# Revit family: Filter für Warmwasser 0554
name_source: partatom
category: Rohrzubehör
units: mm (PartAtom-declared; Revit-internal decimal feet)

## family parameters
Arbeitsebenenbasiert = Nein
Beim Laden mit Abzugskörper schneiden = Nein
Bemaßung runder Anschluss = Durchmesser verwenden
Gemeinsam genutzt = Nein
Immer vertikal = Ja
OmniClass-Nummer = 23.65.55.14
OmniClass-Titel = Valves for Liquid Services
Teiletyp = Unterbricht

## types (1)
- Filter für Warmwasser 0554
    Ausführung = Der HERZ-Wasserfilter wird in Hauseingangsanlagen für Trinkwasser eingesetzt, um das Trinkwasser vor Verunreinigungen zu schützen.
    D01 = 25.5 mm
    D02 = 22.75 mm  [stored 0.0746391 ft]
    Filter = Edelstahl, Maschenweite 100 μm
    Gehäuse = Messing, CW617N
    H01 = 24 mm  [stored 0.0787402 ft]
    H02 = 45.5 mm  [stored 0.149278 ft]
    H03 = 67.5 mm
    H04 = 151 mm
    Hersteller = HERZ Armaturen Ges.m.b.H.
    Hinweis = Gemäß Art 33 der REACH-Verordnung (EG Nr. 1907/2006) sind wir verpflichtet, darauf hinzuweisen, dass der Stoff Blei auf der SVHC-Liste geführt wird und dass alle aus Messing bestehenden Bauteile, die in unseren Erzeugnissen verarbeitet sind, mehr als 0,1 % (w/w) Blei (CAS: 7439-92-1 / EINECS: 231-100-4) enthalten.
Da Blei als Legierungsbestandteil fest gebunden ist, sind keine Expositionen zu erwarten und daher sind keine zusätzlichen Angaben zur sicheren Verwendung notwendig.
    Max. Betriebsdruck = 1600000.0 Pa
    Max. Betriebstemperatur = 60 °C
    Medium = Trinkwasser
    Model = Filter für Heißwasser mit Gehäuse aus Messing und Tasse aus Trogamid.
    R01 = 12.5 mm  [stored 0.0410105 ft]
    R02 = 8 mm  [stored 0.0262467 ft]
    SCTWCODE = 02;00;02
    SCTWSEQ = FI;SBT_TYP_FI="FI";2
    SC_NennweiteBerechnet = 0
    T01 = 1 mm  [stored 0.00328084 ft]
    Tasse = Kunststoff, Trogamid
    URL = www.herz-armaturen.at
    VRS01 = 10 mm  [stored 0.0328084 ft]
    W01 = 89.00°
    W02 = 88.00°

note: [stored X ft] marks values corroborated as IEEE doubles in the binary element streams (Revit-internal decimal feet)
